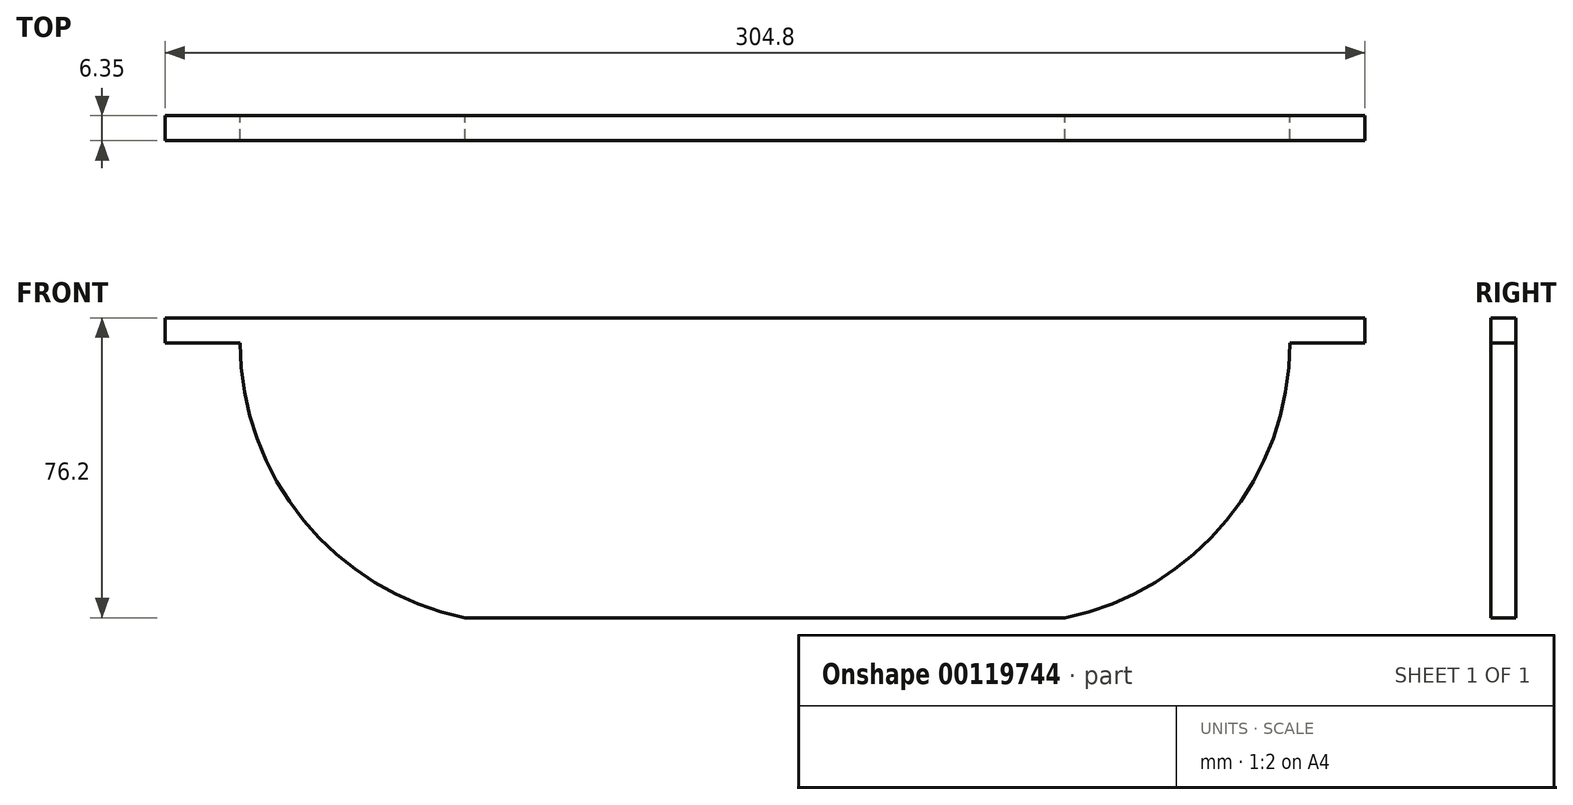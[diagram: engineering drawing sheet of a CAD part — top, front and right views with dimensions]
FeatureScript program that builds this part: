
annotation { "Feature Type Name" : "Feature", "Feature Type Description" : "" }
export const myFeature = defineFeature(function(context is Context, id is Id, definition is map)
    precondition{}
    {
        {
            var Q0;
            Q0=qCreatedBy(makeId("Front.planeOp"),FACE);
            var sketch = newSketch(context, id + "F0", { "sketchPlane" : qUnion([Q0])});
            skLineSegment(sketch, "E0.bottom", {"start": v(-97.4, 0) * mm, "end": v(-72, 0) * mm});
            skLineSegment(sketch, "E0.left", {"start": v(-97.4, 0) * mm, "end": v(-97.4, -6.35) * mm});
            skLineSegment(sketch, "E0.right", {"start": v(169.3, -69.85) * mm, "end": v(169.3, -76.2) * mm});
            skLineSegment(sketch, "E1", {"start": v(-97.4, -6.35) * mm, "end": v(-78.36, -6.35) * mm});
            skPoint(sketch, "E2.orphan", {"position": v(-72, 0) * mm});
            skArc(sketch, "E3", {"start": v(-78.36, -6.35) * mm, "mid": v(-62.25, -51.48) * mm, "end": v(-21.2, -76.2) * mm});
            skLineSegment(sketch, "E4.trimOffspring", {"start": v(-21.2, -76.2) * mm, "end": v(131.2, -76.2) * mm});
            skArc(sketch, "E5.MirrorCS", {"start": v(188.34, -6.35) * mm, "mid": v(172.23, -51.48) * mm, "end": v(131.2, -76.2) * mm});
            skLineSegment(sketch, "E6.MirrorCS", {"start": v(207.4, -6.35) * mm, "end": v(188.34, -6.35) * mm});
            skLineSegment(sketch, "E7.MirrorCS", {"start": v(207.4, 0) * mm, "end": v(182, 0) * mm});
            skLineSegment(sketch, "E8.MirrorCS", {"start": v(207.4, 0) * mm, "end": v(207.4, -6.35) * mm});
            skPoint(sketch, "E9.orphan", {"position": v(169.3, -69.85) * mm});
            skPoint(sketch, "E10.orphan", {"position": v(131.2, -76.2) * mm});
            skPoint(sketch, "E11.start.orphan", {"position": v(-21.2, 0) * mm});
            skPoint(sketch, "E12.start.orphan", {"position": v(55, 0) * mm});
            skLineSegment(sketch, "E13", {"start": v(55, -69.85) * mm, "end": v(55, 90.58) * mm});
            skLineSegment(sketch, "E14", {"start": v(-72, 0) * mm, "end": v(182, 0) * mm});
            skPoint(sketch, "E15.orphan", {"position": v(-21.2, -69.85) * mm});
            skPoint(sketch, "E16.MirrorCS.end.orphan", {"position": v(131.2, -69.85) * mm});
            skPoint(sketch, "E17.end.orphan", {"position": v(-72, -6.35) * mm});
            skSolve(sketch);
        }
        {
            var Q0;
            Q0 = qSketchRegion(id + "F0", true);
            extrude(context, id + "F1", {"entities" : qUnion([Q0]), "depth" : 6.35 * mm});
        }
    });
